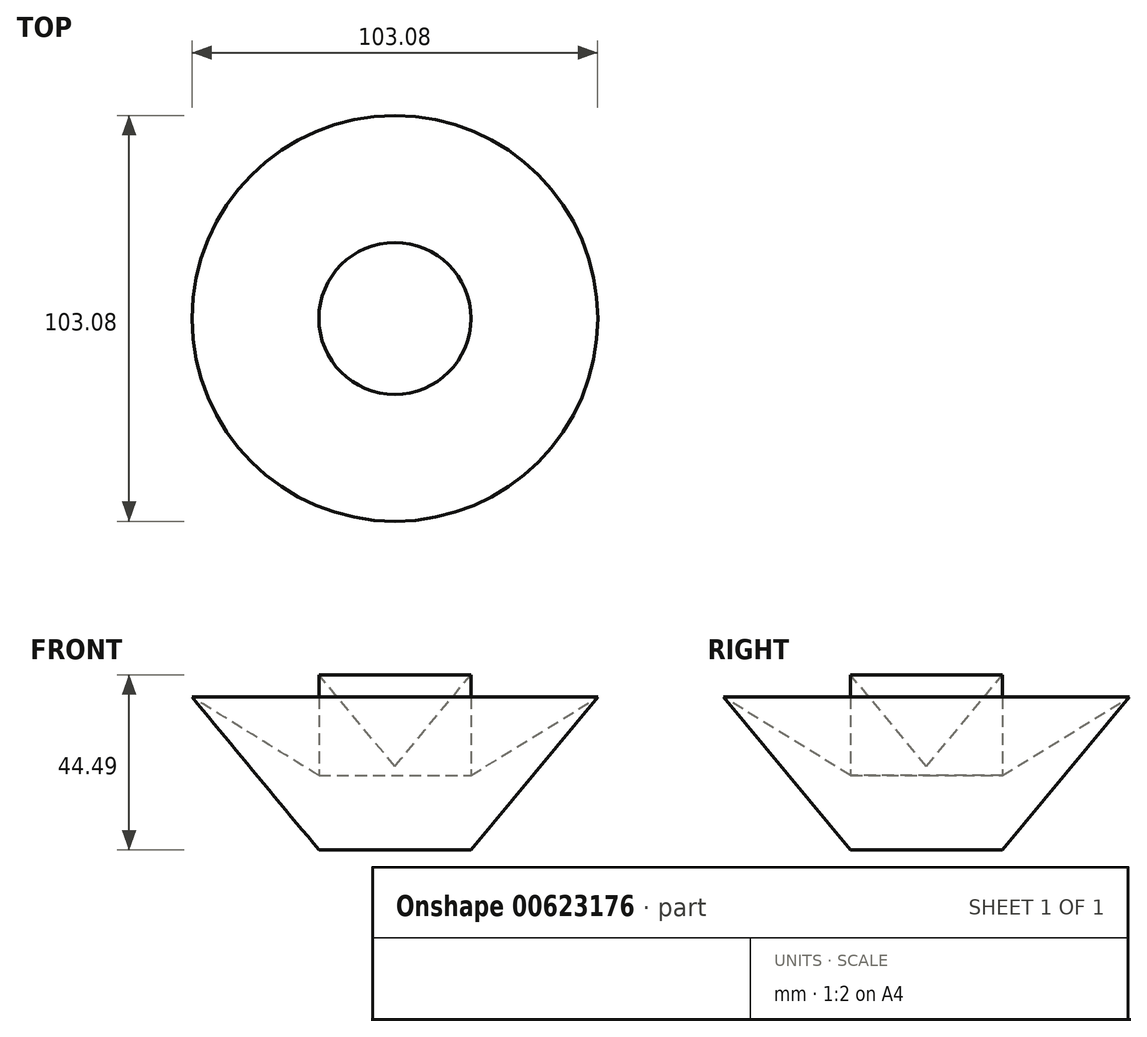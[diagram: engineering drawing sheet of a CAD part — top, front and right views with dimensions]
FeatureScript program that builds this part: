
annotation { "Feature Type Name" : "Feature", "Feature Type Description" : "" }
export const myFeature = defineFeature(function(context is Context, id is Id, definition is map)
    precondition{}
    {
        {
            var Q0;
            Q0=qCreatedBy(makeId("Front.planeOp"),FACE);
            var sketch = newSketch(context, id + "F0", { "sketchPlane" : qUnion([Q0])});
            skLineSegment(sketch, "E0", {"start": v(19.3, 44.49) * mm, "end": v(19.3, 18.88) * mm});
            skLineSegment(sketch, "E1", {"start": v(19.3, 44.49) * mm, "end": v(0, 21.23) * mm});
            skLineSegment(sketch, "E2", {"start": v(19.3, 0) * mm, "end": v(0, 0) * mm});
            skLineSegment(sketch, "E3", {"start": v(19.3, 0) * mm, "end": v(51.54, 38.82) * mm});
            skLineSegment(sketch, "E4", {"start": v(51.54, 38.82) * mm, "end": v(19.3, 18.88) * mm});
            skLineSegment(sketch, "E5", {"start": v(0, 0) * mm, "end": v(0, 21.23) * mm});
            skSolve(sketch);
        }
        {
            var Q0;
            Q0 = qSketchRegion(id + "F0", true);
            var Q1;
            Q1=sQuery(id+"F0.wireOp",EDGE,"E5");
            revolve(context, id + "F1", {"entities" : qUnion([Q0]), "axis" : qUnion([Q1]), "revolveType" : RevolveType.FULL});
        }
    });
